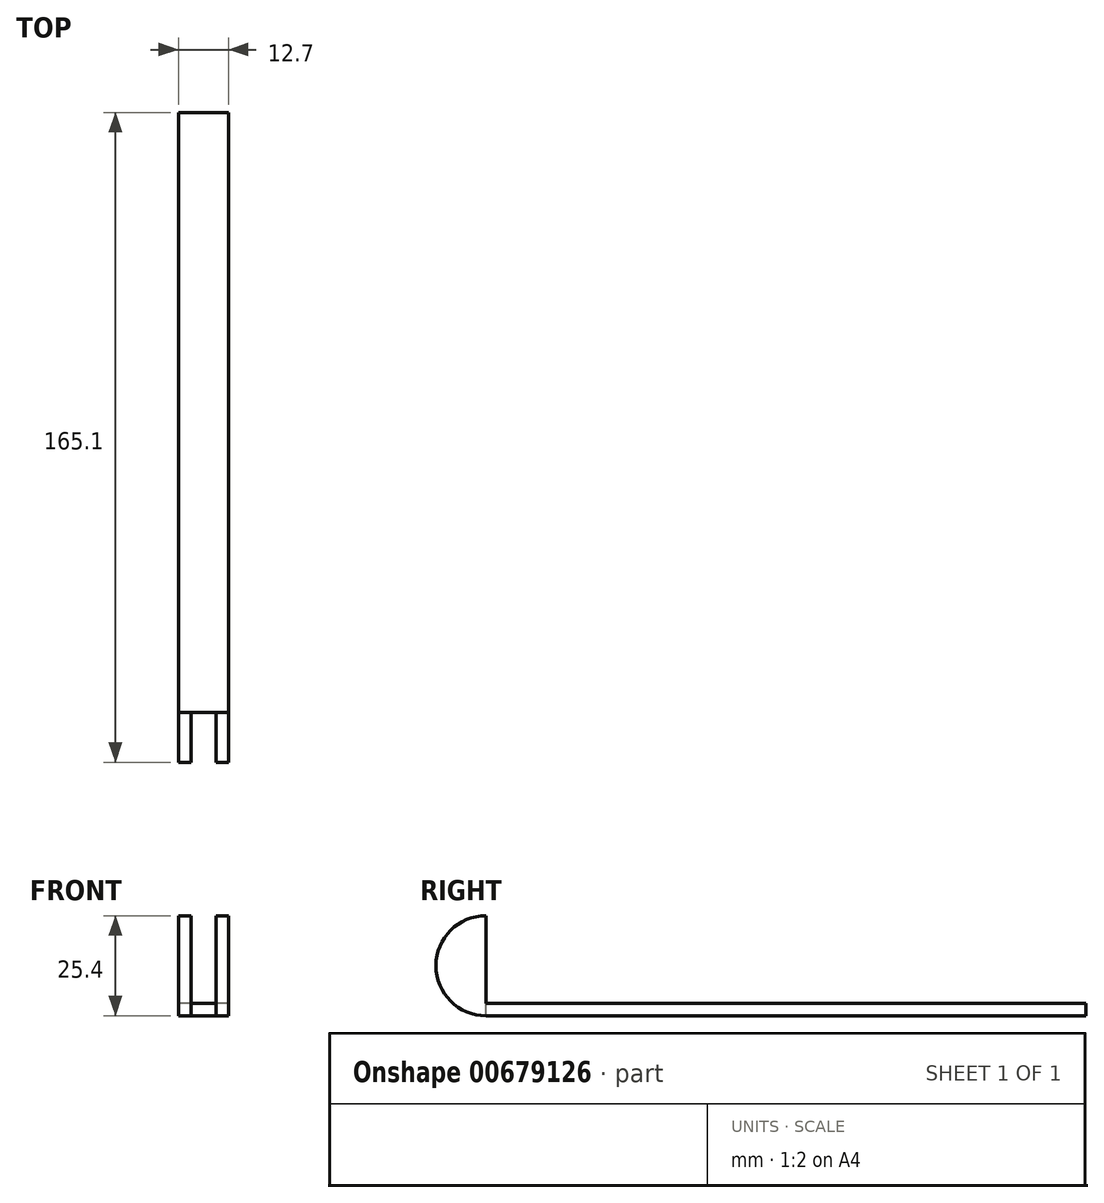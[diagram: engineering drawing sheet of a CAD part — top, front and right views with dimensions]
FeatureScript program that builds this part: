
annotation { "Feature Type Name" : "Feature", "Feature Type Description" : "" }
export const myFeature = defineFeature(function(context is Context, id is Id, definition is map)
    precondition{}
    {
        {
            var Q0;
            Q0=qCreatedBy(makeId("Right.planeOp"),FACE);
            var sketch = newSketch(context, id + "F0", { "sketchPlane" : qUnion([Q0])});
            skLineSegment(sketch, "E0.bottom", {"start": v(0, 0) * mm, "end": v(177.8, 0) * mm});
            skLineSegment(sketch, "E0.top", {"start": v(0, 38.1) * mm, "end": v(177.8, 38.1) * mm});
            skLineSegment(sketch, "E0.left", {"start": v(0, 0) * mm, "end": v(0, 38.1) * mm});
            skLineSegment(sketch, "E0.right", {"start": v(177.8, 0) * mm, "end": v(177.8, 38.1) * mm});
            skArc(sketch, "E1", {"start": v(0, 38.1) * mm, "mid": v(88.9, 24.85) * mm, "end": v(177.8, 38.1) * mm});
            skLineSegment(sketch, "E2.bottom", {"start": v(0, 0) * mm, "end": v(12.7, 0) * mm});
            skLineSegment(sketch, "E2.top", {"start": v(0, 25.4) * mm, "end": v(12.7, 25.4) * mm});
            skLineSegment(sketch, "E2.left", {"start": v(0, 0) * mm, "end": v(0, 25.4) * mm});
            skLineSegment(sketch, "E2.right", {"start": v(12.7, 0) * mm, "end": v(12.7, 25.4) * mm});
            skLineSegment(sketch, "E3.bottom", {"start": v(177.8, 0) * mm, "end": v(165.1, 0) * mm});
            skLineSegment(sketch, "E3.top", {"start": v(177.8, 25.4) * mm, "end": v(165.1, 25.4) * mm});
            skLineSegment(sketch, "E3.left", {"start": v(177.8, 0) * mm, "end": v(177.8, 25.4) * mm});
            skLineSegment(sketch, "E3.right", {"start": v(165.1, 0) * mm, "end": v(165.1, 25.4) * mm});
            skLineSegment(sketch, "E4", {"start": v(12.7, 3.18) * mm, "end": v(165.1, 3.18) * mm});
            skSolve(sketch);
        }
        {
            var Q0;
            Q0=makeQuery(id+"F0.imprint","IMPRINT",FACE,{"disambiguationData":[TD([[makeQuery(id+"F0.imprint","IMPRINT",EDGE,{"derivedFrom":sQuery(id+"F0.wireOp",EDGE,"E0.bottom")}),1.0]])]});
            var Q1;
            Q1=makeQuery(id+"F0.imprint","IMPRINT",FACE,{"disambiguationData":[TD([[makeQuery(id+"F0.imprint","IMPRINT",EDGE,{"derivedFrom":sQuery(id+"F0.wireOp",EDGE,"E2.bottom")}),1.0]])]});
            var Q2;
            Q2=makeQuery(id+"F0.imprint","IMPRINT",FACE,{"disambiguationData":[TD([[makeQuery(id+"F0.imprint","IMPRINT",EDGE,{"derivedFrom":sQuery(id+"F0.wireOp",EDGE,"E3.bottom")}),-1.0]])]});
            var Q3;
            Q3=makeQuery(id+"F0.imprint","IMPRINT",FACE,{"disambiguationData":[TD([[makeQuery(id+"F0.imprint","IMPRINT",EDGE,{"derivedFrom":sQuery(id+"F0.wireOp",EDGE,"E0.left")}),-1.0]])]});
            extrude(context, id + "F1", {"entities" : qUnion([Q0, Q1, Q2, Q3]), "endBound" : BoundingType.SYMMETRIC, "depth" : 12.7 * mm, "offsetDistance" : 25.4 * mm});
        }
        {
            var Q0;
            Q0=makeQuery(id+"F0.imprint","IMPRINT",FACE,{"disambiguationData":[TD([[makeQuery(id+"F0.imprint","IMPRINT",EDGE,{"derivedFrom":sQuery(id+"F0.wireOp",EDGE,"E0.left")}),-1.0]])]});
            extrude(context, id + "F2", {"entities" : qUnion([Q0]), "operationType" : NewBodyOperationType.REMOVE, "endBound" : BoundingType.SYMMETRIC, "depth" : 6.35 * mm, "offsetDistance" : 25.4 * mm});
        }
        {
            var Q0;
            {var subQ0=sQuery(id+"F0.wireOp",EDGE,"E2.left");var subQ1=sQuery(id+"F0.wireOp",EDGE,"E1");var subQ2=sQuery(id+"F0.wireOp",EDGE,"E0.right");var subQ3=sQuery(id+"F0.wireOp",EDGE,"E0.left");Q0=makeQuery(id+"F2.boolean.opBoolean","SPLIT",EDGE,{"disambiguationData":[TD([makeQuery(id+"F1.opExtrude","CAP_FACE",FACE,{"disambiguationData":[OSD([sQuery(id+"F0.wireOp",EDGE,"E0.bottom"),subQ3,subQ2,subQ1,sQuery(id+"F0.wireOp",EDGE,"E2.bottom"),subQ0,sQuery(id+"F0.wireOp",EDGE,"E3.bottom"),sQuery(id+"F0.wireOp",EDGE,"E3.left")])],"isStart":true})])],"derivedFrom":makeQuery(id+"F1.opExtrude","SWEPT_EDGE",EDGE,{"disambiguationData":[OSD([sQuery(id+"F0.wireOp",EDGE,"E0.top"),subQ3,subQ1])]})});}
            var Q1;
            {var subQ0=sQuery(id+"F0.wireOp",EDGE,"E2.left");var subQ1=sQuery(id+"F0.wireOp",EDGE,"E1");var subQ2=sQuery(id+"F0.wireOp",EDGE,"E0.right");var subQ3=sQuery(id+"F0.wireOp",EDGE,"E0.left");Q1=makeQuery(id+"F2.boolean.opBoolean","SPLIT",EDGE,{"disambiguationData":[TD([makeQuery(id+"F1.opExtrude","CAP_FACE",FACE,{"disambiguationData":[OSD([sQuery(id+"F0.wireOp",EDGE,"E0.bottom"),subQ3,subQ2,subQ1,sQuery(id+"F0.wireOp",EDGE,"E2.bottom"),subQ0,sQuery(id+"F0.wireOp",EDGE,"E3.bottom"),sQuery(id+"F0.wireOp",EDGE,"E3.left")])],"isStart":false})])],"derivedFrom":makeQuery(id+"F1.opExtrude","SWEPT_EDGE",EDGE,{"disambiguationData":[OSD([sQuery(id+"F0.wireOp",EDGE,"E0.top"),subQ3,subQ1])]})});}
            var Q2;
            {var subQ0=sQuery(id+"F0.wireOp",EDGE,"E3.left");var subQ1=sQuery(id+"F0.wireOp",EDGE,"E1");var subQ2=sQuery(id+"F0.wireOp",EDGE,"E0.right");var subQ3=sQuery(id+"F0.wireOp",EDGE,"E0.left");Q2=makeQuery(id+"F2.boolean.opBoolean","SPLIT",EDGE,{"disambiguationData":[TD([makeQuery(id+"F1.opExtrude","CAP_FACE",FACE,{"disambiguationData":[OSD([sQuery(id+"F0.wireOp",EDGE,"E0.bottom"),subQ3,subQ2,subQ1,sQuery(id+"F0.wireOp",EDGE,"E2.bottom"),sQuery(id+"F0.wireOp",EDGE,"E2.left"),sQuery(id+"F0.wireOp",EDGE,"E3.bottom"),subQ0])],"isStart":true})])],"derivedFrom":makeQuery(id+"F1.opExtrude","SWEPT_EDGE",EDGE,{"disambiguationData":[OSD([sQuery(id+"F0.wireOp",EDGE,"E0.top"),subQ2,subQ1])]})});}
            var Q3;
            {var subQ0=sQuery(id+"F0.wireOp",EDGE,"E3.left");var subQ1=sQuery(id+"F0.wireOp",EDGE,"E1");var subQ2=sQuery(id+"F0.wireOp",EDGE,"E0.right");var subQ3=sQuery(id+"F0.wireOp",EDGE,"E0.left");Q3=makeQuery(id+"F2.boolean.opBoolean","SPLIT",EDGE,{"disambiguationData":[TD([makeQuery(id+"F1.opExtrude","CAP_FACE",FACE,{"disambiguationData":[OSD([sQuery(id+"F0.wireOp",EDGE,"E0.bottom"),subQ3,subQ2,subQ1,sQuery(id+"F0.wireOp",EDGE,"E2.bottom"),sQuery(id+"F0.wireOp",EDGE,"E2.left"),sQuery(id+"F0.wireOp",EDGE,"E3.bottom"),subQ0])],"isStart":false})])],"derivedFrom":makeQuery(id+"F1.opExtrude","SWEPT_EDGE",EDGE,{"disambiguationData":[OSD([sQuery(id+"F0.wireOp",EDGE,"E0.top"),subQ2,subQ1])]})});}
            fillet(context, id + "F3", {"entities" : qUnion([Q0, Q1, Q2, Q3]), "radius" : 12.7 * mm, "tangentPropagation" : true, "allowEdgeOverflow" : false});
        }
    });
